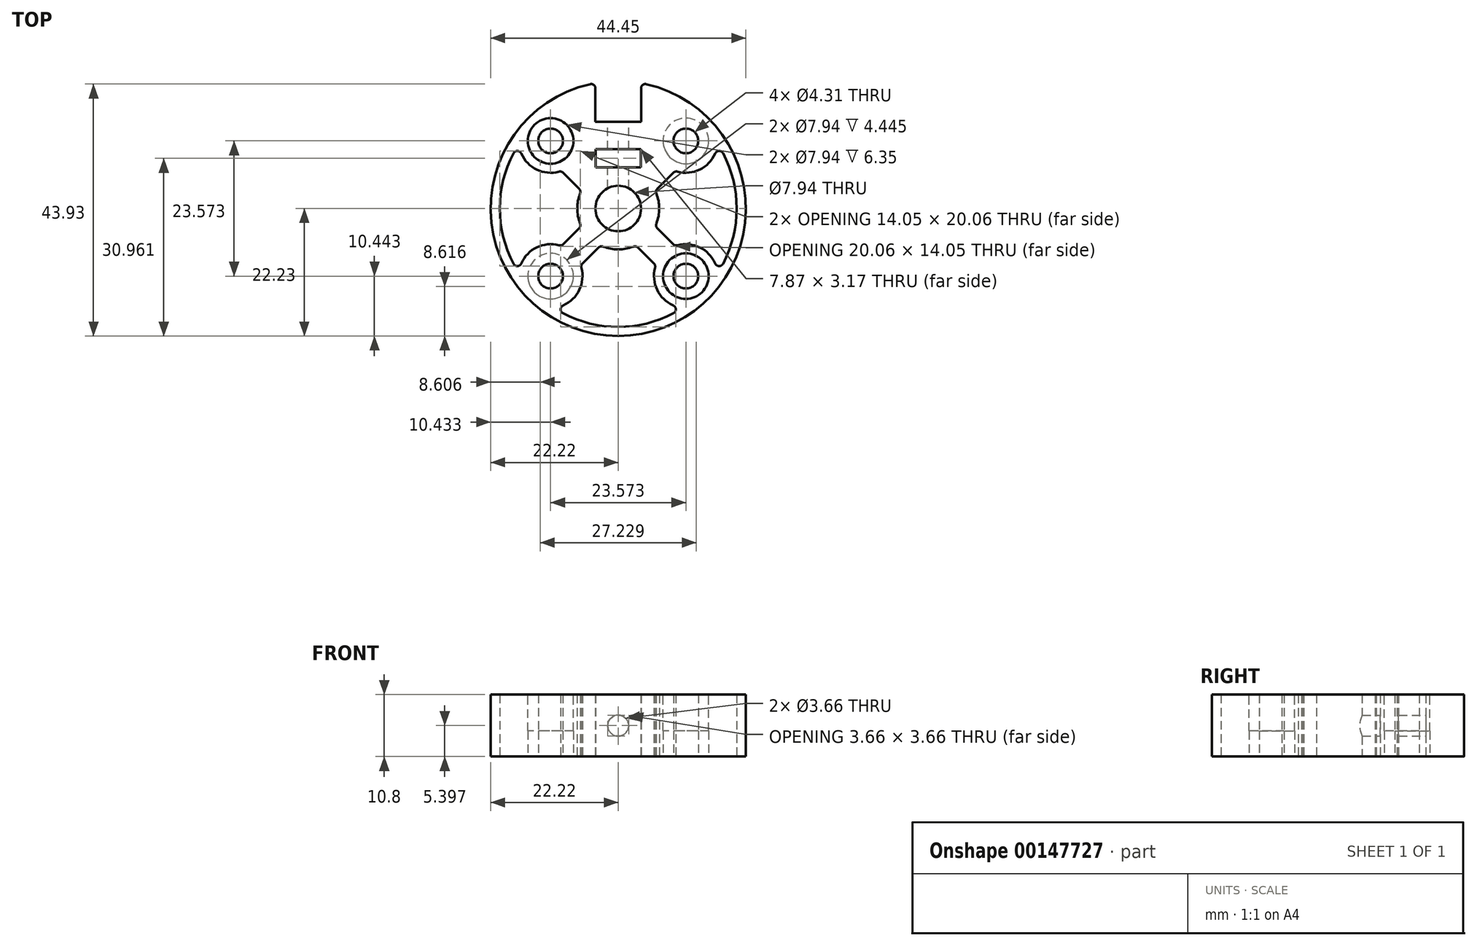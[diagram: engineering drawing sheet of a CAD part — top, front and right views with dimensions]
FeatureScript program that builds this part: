
annotation { "Feature Type Name" : "Feature", "Feature Type Description" : "" }
export const myFeature = defineFeature(function(context is Context, id is Id, definition is map)
    precondition{}
    {
        {
            var Q0;
            Q0=qCreatedBy(makeId("Top.planeOp"),FACE);
            var sketch = newSketch(context, id + "F0", { "sketchPlane" : qUnion([Q0])});
            skCircle(sketch, "E0", {"center": v(0, 0) * mm, "radius": 3.97 * mm});
            skLineSegment(sketch, "E1.bottom", {"start": v(11.79, 11.79) * mm, "end": v(-11.79, 11.79) * mm, "construction": true});
            skLineSegment(sketch, "E1.top", {"start": v(11.79, -11.79) * mm, "end": v(-11.79, -11.79) * mm, "construction": true});
            skLineSegment(sketch, "E1.left", {"start": v(11.79, 11.79) * mm, "end": v(11.79, -11.79) * mm, "construction": true});
            skLineSegment(sketch, "E1.right", {"start": v(-11.79, 11.79) * mm, "end": v(-11.79, -11.79) * mm, "construction": true});
            skCircle(sketch, "E2", {"center": v(-11.79, 11.79) * mm, "radius": 5.56 * mm, "construction": true});
            skLineSegment(sketch, "E3.bottom", {"start": v(-3.97, 21.87) * mm, "end": v(3.97, 21.87) * mm, "construction": true});
            skLineSegment(sketch, "E3.top", {"start": v(-3.97, 15.08) * mm, "end": v(3.97, 15.08) * mm});
            skLineSegment(sketch, "E3.left", {"start": v(-3.97, 21.87) * mm, "end": v(-3.97, 15.08) * mm});
            skLineSegment(sketch, "E3.right", {"start": v(3.97, 21.87) * mm, "end": v(3.97, 15.08) * mm});
            skArc(sketch, "E4", {"start": v(-3.97, 21.87) * mm, "mid": v(0, -22.22) * mm, "end": v(3.97, 21.87) * mm});
            skCircle(sketch, "E5", {"center": v(-11.79, 11.79) * mm, "radius": 2.15 * mm});
            skCircle(sketch, "E6", {"center": v(-11.79, -11.79) * mm, "radius": 2.15 * mm});
            skCircle(sketch, "E7", {"center": v(11.79, -11.79) * mm, "radius": 2.15 * mm});
            skCircle(sketch, "E8", {"center": v(11.79, 11.79) * mm, "radius": 2.15 * mm});
            skLineSegment(sketch, "E9", {"start": v(0, 15.08) * mm, "end": v(0, 10.32) * mm, "construction": true});
            skLineSegment(sketch, "E10", {"start": v(0, 0) * mm, "end": v(0, 2.38) * mm, "construction": true});
            skLineSegment(sketch, "E11", {"start": v(0, 2.38) * mm, "end": v(0, 3.97) * mm, "construction": true});
            skLineSegment(sketch, "E12", {"start": v(0, 3.97) * mm, "end": v(0, 7.14) * mm, "construction": true});
            skLineSegment(sketch, "E13.bottom", {"start": v(3.94, 10.32) * mm, "end": v(-3.94, 10.32) * mm});
            skLineSegment(sketch, "E13.top", {"start": v(3.94, 7.14) * mm, "end": v(-3.94, 7.14) * mm});
            skLineSegment(sketch, "E13.left", {"start": v(3.94, 10.32) * mm, "end": v(3.94, 7.14) * mm});
            skLineSegment(sketch, "E13.right", {"start": v(-3.94, 10.32) * mm, "end": v(-3.94, 7.14) * mm});
            skSolve(sketch);
        }
        {
            var Q0;
            Q0=qSketchRegion(id+"F0",true);
            extrude(context, id + "F1", {"entities" : qUnion([Q0]), "depth" : 10.8 * mm});
        }
        {
            var Q0;
            Q0=makeQuery(id+"F1.opExtrude","SWEPT_FACE",FACE,{"disambiguationData":[OSD([sQuery(id+"F0.wireOp",EDGE,"E3.top")])]});
            var sketch = newSketch(context, id + "F2", { "sketchPlane" : qUnion([Q0])});
            skLineSegment(sketch, "E14", {"start": v(0, 10.8) * mm, "end": v(0, 0) * mm, "construction": true});
            skCircle(sketch, "E15", {"center": v(0, 5.4) * mm, "radius": 1.83 * mm});
            skSolve(sketch);
        }
        {
            var Q0;
            Q0=qSketchRegion(id+"F2",true);
            var Q1;
            Q1=makeQuery(id+"F1.opExtrude","SWEPT_FACE",FACE,{"disambiguationData":[OSD([sQuery(id+"F0.wireOp",EDGE,"E0")])]});
            extrude(context, id + "F3", {"entities" : qUnion([Q0]), "operationType" : NewBodyOperationType.REMOVE, "endBound" : BoundingType.UP_TO_SURFACE, "oppositeDirection" : true, "endBoundEntityFace" : qUnion([Q1]), "depth" : 25.4 * mm});
        }
        {
            var Q0;
            Q0=makeQuery(id+"F1.opExtrude","CAP_FACE",FACE,{"disambiguationData":[OSD([sQuery(id+"F0.wireOp",EDGE,"E0"),sQuery(id+"F0.wireOp",EDGE,"E3.top"),sQuery(id+"F0.wireOp",EDGE,"E3.left"),sQuery(id+"F0.wireOp",EDGE,"E3.right"),sQuery(id+"F0.wireOp",EDGE,"E4"),sQuery(id+"F0.wireOp",EDGE,"E5"),sQuery(id+"F0.wireOp",EDGE,"E6"),sQuery(id+"F0.wireOp",EDGE,"E7"),sQuery(id+"F0.wireOp",EDGE,"E8")])],"isStart":false});
            cPlane(context, id + "F4", {"entities" : qUnion([Q0]), "cplaneType" : CPlaneType.OFFSET, "offset" : 6.35 * mm, "oppositeDirection" : true, "width" : 152.4 * mm, "height" : 152.4 * mm});
        }
        {
            var Q0;
            Q0=makeQuery(id+"F1.opExtrude","CAP_FACE",FACE,{"disambiguationData":[OSD([sQuery(id+"F0.wireOp",EDGE,"E0"),sQuery(id+"F0.wireOp",EDGE,"E3.top"),sQuery(id+"F0.wireOp",EDGE,"E3.left"),sQuery(id+"F0.wireOp",EDGE,"E3.right"),sQuery(id+"F0.wireOp",EDGE,"E4"),sQuery(id+"F0.wireOp",EDGE,"E5"),sQuery(id+"F0.wireOp",EDGE,"E6"),sQuery(id+"F0.wireOp",EDGE,"E7"),sQuery(id+"F0.wireOp",EDGE,"E8")])],"isStart":true});
            var sketch = newSketch(context, id + "F5", { "sketchPlane" : qUnion([Q0])});
            skCircle(sketch, "E16", {"center": v(11.79, -11.79) * mm, "radius": 3.97 * mm});
            skCircle(sketch, "E17", {"center": v(-11.79, 11.79) * mm, "radius": 3.97 * mm});
            skSolve(sketch);
        }
        {
            var Q0;
            Q0=qSketchRegion(id+"F5",true);
            var Q1;
            Q1=qCreatedBy(id+"F4.planeOp",FACE);
            extrude(context, id + "F6", {"entities" : qUnion([Q0]), "operationType" : NewBodyOperationType.REMOVE, "endBound" : BoundingType.UP_TO_SURFACE, "oppositeDirection" : true, "endBoundEntityFace" : qUnion([Q1]), "depth" : 25.4 * mm});
        }
        {
            var Q0;
            Q0=makeQuery(id+"F1.opExtrude","CAP_FACE",FACE,{"disambiguationData":[OSD([sQuery(id+"F0.wireOp",EDGE,"E0"),sQuery(id+"F0.wireOp",EDGE,"E3.top"),sQuery(id+"F0.wireOp",EDGE,"E3.left"),sQuery(id+"F0.wireOp",EDGE,"E3.right"),sQuery(id+"F0.wireOp",EDGE,"E4"),sQuery(id+"F0.wireOp",EDGE,"E5"),sQuery(id+"F0.wireOp",EDGE,"E6"),sQuery(id+"F0.wireOp",EDGE,"E7"),sQuery(id+"F0.wireOp",EDGE,"E8")])],"isStart":true});
            var sketch = newSketch(context, id + "F7", { "sketchPlane" : qUnion([Q0])});
            skArc(sketch, "E18", {"start": v(-9.92, -6.55) * mm, "mid": v(-14.76, -7.1) * mm, "end": v(-17.31, -11.23) * mm});
            skArc(sketch, "E19", {"start": v(-17.31, 11.23) * mm, "mid": v(-14.76, 7.1) * mm, "end": v(-9.92, 6.55) * mm});
            skArc(sketch, "E20", {"start": v(-17.31, 11.23) * mm, "mid": v(-20.64, 0) * mm, "end": v(-17.31, -11.23) * mm});
            skLineSegment(sketch, "E21", {"start": v(-11.79, 11.79) * mm, "end": v(-8.24, 8.24) * mm, "construction": true});
            skLineSegment(sketch, "E22", {"start": v(-11.79, -11.79) * mm, "end": v(-8.24, -8.24) * mm, "construction": true});
            skLineSegment(sketch, "E23", {"start": v(0, 0) * mm, "end": v(-4.76, 4.76) * mm, "construction": true});
            skLineSegment(sketch, "E24", {"start": v(0, 0) * mm, "end": v(-4.76, -4.76) * mm, "construction": true});
            skLineSegment(sketch, "E25.bottom", {"start": v(-6.45, 3.08) * mm, "end": v(-9.92, 6.55) * mm});
            skLineSegment(sketch, "E25.top", {"start": v(-3.08, 6.45) * mm, "end": v(-6.55, 9.92) * mm, "construction": true});
            skLineSegment(sketch, "E25.left", {"start": v(-6.45, 3.08) * mm, "end": v(-3.08, 6.45) * mm, "construction": true});
            skLineSegment(sketch, "E25.right", {"start": v(-9.92, 6.55) * mm, "end": v(-6.55, 9.92) * mm, "construction": true});
            skLineSegment(sketch, "E26.bottom", {"start": v(-6.45, -3.08) * mm, "end": v(-9.92, -6.55) * mm});
            skLineSegment(sketch, "E26.top", {"start": v(-3.08, -6.45) * mm, "end": v(-6.55, -9.92) * mm, "construction": true});
            skLineSegment(sketch, "E26.left", {"start": v(-6.45, -3.08) * mm, "end": v(-3.08, -6.45) * mm, "construction": true});
            skLineSegment(sketch, "E26.right", {"start": v(-9.92, -6.55) * mm, "end": v(-6.55, -9.92) * mm, "construction": true});
            skArc(sketch, "E27", {"start": v(-6.45, 3.08) * mm, "mid": v(-7.14, 0) * mm, "end": v(-6.45, -3.08) * mm});
            skSolve(sketch);
        }
        {
            var Q0;
            Q0=qSketchRegion(id+"F7",true);
            var Q1;
            Q1=makeQuery(id+"F1.opExtrude","CAP_FACE",FACE,{"disambiguationData":[OSD([sQuery(id+"F0.wireOp",EDGE,"E0"),sQuery(id+"F0.wireOp",EDGE,"E3.top"),sQuery(id+"F0.wireOp",EDGE,"E3.left"),sQuery(id+"F0.wireOp",EDGE,"E3.right"),sQuery(id+"F0.wireOp",EDGE,"E4"),sQuery(id+"F0.wireOp",EDGE,"E5"),sQuery(id+"F0.wireOp",EDGE,"E6"),sQuery(id+"F0.wireOp",EDGE,"E7"),sQuery(id+"F0.wireOp",EDGE,"E8")])],"isStart":false});
            extrude(context, id + "F8", {"entities" : qUnion([Q0]), "operationType" : NewBodyOperationType.REMOVE, "endBound" : BoundingType.UP_TO_SURFACE, "oppositeDirection" : true, "endBoundEntityFace" : qUnion([Q1]), "depth" : 25.4 * mm});
        }
        {
            var Q0;
            Q0=makeQuery(id+"F8.boolean.opBoolean","COPY",EDGE,{"derivedFrom":makeQuery(id+"F8.opExtrude","SWEPT_EDGE",EDGE,{"disambiguationData":[OSD([sQuery(id+"F7.wireOp",EDGE,"E19"),sQuery(id+"F7.wireOp",EDGE,"E20")])]})});
            var Q1;
            Q1=makeQuery(id+"F8.boolean.opBoolean","COPY",EDGE,{"derivedFrom":makeQuery(id+"F8.opExtrude","SWEPT_EDGE",EDGE,{"disambiguationData":[OSD([sQuery(id+"F7.wireOp",EDGE,"E19"),sQuery(id+"F7.wireOp",EDGE,"E25.bottom")])]})});
            var Q2;
            Q2=makeQuery(id+"F8.boolean.opBoolean","COPY",EDGE,{"derivedFrom":makeQuery(id+"F8.opExtrude","SWEPT_EDGE",EDGE,{"disambiguationData":[OSD([sQuery(id+"F7.wireOp",EDGE,"E25.bottom"),sQuery(id+"F7.wireOp",EDGE,"E27")])]})});
            var Q3;
            Q3=makeQuery(id+"F8.boolean.opBoolean","COPY",EDGE,{"derivedFrom":makeQuery(id+"F8.opExtrude","SWEPT_EDGE",EDGE,{"disambiguationData":[OSD([sQuery(id+"F7.wireOp",EDGE,"E26.bottom"),sQuery(id+"F7.wireOp",EDGE,"E27")])]})});
            var Q4;
            Q4=makeQuery(id+"F8.boolean.opBoolean","COPY",EDGE,{"derivedFrom":makeQuery(id+"F8.opExtrude","SWEPT_EDGE",EDGE,{"disambiguationData":[OSD([sQuery(id+"F7.wireOp",EDGE,"E18"),sQuery(id+"F7.wireOp",EDGE,"E26.bottom")])]})});
            var Q5;
            Q5=makeQuery(id+"F8.boolean.opBoolean","COPY",EDGE,{"derivedFrom":makeQuery(id+"F8.opExtrude","SWEPT_EDGE",EDGE,{"disambiguationData":[OSD([sQuery(id+"F7.wireOp",EDGE,"E18"),sQuery(id+"F7.wireOp",EDGE,"E20")])]})});
            var Q6;
            Q6=makeQuery(id+"F1.opExtrude","SWEPT_EDGE",EDGE,{"disambiguationData":[OSD([sQuery(id+"F0.wireOp",EDGE,"E3.right"),sQuery(id+"F0.wireOp",EDGE,"E4")])]});
            var Q7;
            Q7=makeQuery(id+"F1.opExtrude","SWEPT_EDGE",EDGE,{"disambiguationData":[OSD([sQuery(id+"F0.wireOp",EDGE,"E3.left"),sQuery(id+"F0.wireOp",EDGE,"E4")])]});
            fillet(context, id + "F9", {"entities" : qUnion([Q0, Q1, Q2, Q3, Q4, Q5, Q6, Q7]), "radius" : 0.76 * mm, "tangentPropagation" : true, "allowEdgeOverflow" : false});
        }
        {
            var Q0;
            Q0=makeQuery(id+"F9.opFillet","BLEND_FACE",FACE,{"disambiguationData":[OSD([sQuery(id+"F7.wireOp",EDGE,"E19"),sQuery(id+"F7.wireOp",EDGE,"E25.bottom")])]});
            var Q1;
            Q1=makeQuery(id+"F8.boolean.opBoolean","COPY",FACE,{"derivedFrom":makeQuery(id+"F8.opExtrude","SWEPT_FACE",FACE,{"disambiguationData":[OSD([sQuery(id+"F7.wireOp",EDGE,"E25.bottom")])]})});
            var Q2;
            Q2=makeQuery(id+"F9.opFillet","BLEND_FACE",FACE,{"disambiguationData":[OSD([sQuery(id+"F7.wireOp",EDGE,"E25.bottom"),sQuery(id+"F7.wireOp",EDGE,"E27")])]});
            var Q3;
            Q3=makeQuery(id+"F8.boolean.opBoolean","COPY",FACE,{"derivedFrom":makeQuery(id+"F8.opExtrude","SWEPT_FACE",FACE,{"disambiguationData":[OSD([sQuery(id+"F7.wireOp",EDGE,"E27")])]})});
            var Q4;
            Q4=makeQuery(id+"F9.opFillet","BLEND_FACE",FACE,{"disambiguationData":[OSD([sQuery(id+"F7.wireOp",EDGE,"E26.bottom"),sQuery(id+"F7.wireOp",EDGE,"E27")])]});
            var Q5;
            Q5=makeQuery(id+"F8.boolean.opBoolean","COPY",FACE,{"derivedFrom":makeQuery(id+"F8.opExtrude","SWEPT_FACE",FACE,{"disambiguationData":[OSD([sQuery(id+"F7.wireOp",EDGE,"E26.bottom")])]})});
            var Q6;
            Q6=makeQuery(id+"F9.opFillet","BLEND_FACE",FACE,{"disambiguationData":[OSD([sQuery(id+"F7.wireOp",EDGE,"E18"),sQuery(id+"F7.wireOp",EDGE,"E26.bottom")])]});
            var Q7;
            Q7=makeQuery(id+"F8.boolean.opBoolean","COPY",FACE,{"derivedFrom":makeQuery(id+"F8.opExtrude","SWEPT_FACE",FACE,{"disambiguationData":[OSD([sQuery(id+"F7.wireOp",EDGE,"E18")])]})});
            var Q8;
            Q8=makeQuery(id+"F9.opFillet","BLEND_FACE",FACE,{"disambiguationData":[OSD([sQuery(id+"F7.wireOp",EDGE,"E18"),sQuery(id+"F7.wireOp",EDGE,"E20")])]});
            var Q9;
            Q9=makeQuery(id+"F8.boolean.opBoolean","COPY",FACE,{"derivedFrom":makeQuery(id+"F8.opExtrude","SWEPT_FACE",FACE,{"disambiguationData":[OSD([sQuery(id+"F7.wireOp",EDGE,"E20")])]})});
            var Q10;
            Q10=makeQuery(id+"F9.opFillet","BLEND_FACE",FACE,{"disambiguationData":[OSD([sQuery(id+"F7.wireOp",EDGE,"E19"),sQuery(id+"F7.wireOp",EDGE,"E20")])]});
            var Q11;
            Q11=makeQuery(id+"F8.boolean.opBoolean","COPY",FACE,{"derivedFrom":makeQuery(id+"F8.opExtrude","SWEPT_FACE",FACE,{"disambiguationData":[OSD([sQuery(id+"F7.wireOp",EDGE,"E19")])]})});
            var Q12;
            Q12=makeQuery(id+"F1.opExtrude","SWEPT_FACE",FACE,{"disambiguationData":[OSD([sQuery(id+"F0.wireOp",EDGE,"E0")])]});
            circularPattern(context, id + "F10", {"patternType" : PatternType.FACE, "faces" : qUnion([Q0, Q1, Q2, Q3, Q4, Q5, Q6, Q7, Q8, Q9, Q10, Q11]), "axis" : qUnion([Q12]), "angle" : 90 * degree, "instanceCount" : 3});
        }
        {
            var Q0;
            Q0=makeQuery(id+"F1.opExtrude","CAP_FACE",FACE,{"disambiguationData":[OSD([sQuery(id+"F0.wireOp",EDGE,"E0"),sQuery(id+"F0.wireOp",EDGE,"E3.top"),sQuery(id+"F0.wireOp",EDGE,"E3.left"),sQuery(id+"F0.wireOp",EDGE,"E3.right"),sQuery(id+"F0.wireOp",EDGE,"E4"),sQuery(id+"F0.wireOp",EDGE,"E5"),sQuery(id+"F0.wireOp",EDGE,"E6"),sQuery(id+"F0.wireOp",EDGE,"E7"),sQuery(id+"F0.wireOp",EDGE,"E8"),sQuery(id+"F0.wireOp",EDGE,"E13.bottom"),sQuery(id+"F0.wireOp",EDGE,"E13.top"),sQuery(id+"F0.wireOp",EDGE,"E13.left"),sQuery(id+"F0.wireOp",EDGE,"E13.right")])],"isStart":false});
            var sketch = newSketch(context, id + "F11", { "sketchPlane" : qUnion([Q0])});
            skCircle(sketch, "E28", {"center": v(-11.79, 11.79) * mm, "radius": 3.97 * mm});
            skCircle(sketch, "E29", {"center": v(11.79, -11.79) * mm, "radius": 3.97 * mm});
            skSolve(sketch);
        }
        {
            var Q0;
            Q0=makeQuery(id+"F1.opExtrude","CAP_FACE",FACE,{"disambiguationData":[OSD([sQuery(id+"F0.wireOp",EDGE,"E0"),sQuery(id+"F0.wireOp",EDGE,"E3.top"),sQuery(id+"F0.wireOp",EDGE,"E3.left"),sQuery(id+"F0.wireOp",EDGE,"E3.right"),sQuery(id+"F0.wireOp",EDGE,"E4"),sQuery(id+"F0.wireOp",EDGE,"E5"),sQuery(id+"F0.wireOp",EDGE,"E6"),sQuery(id+"F0.wireOp",EDGE,"E7"),sQuery(id+"F0.wireOp",EDGE,"E8"),sQuery(id+"F0.wireOp",EDGE,"E13.bottom"),sQuery(id+"F0.wireOp",EDGE,"E13.top"),sQuery(id+"F0.wireOp",EDGE,"E13.left"),sQuery(id+"F0.wireOp",EDGE,"E13.right")])],"isStart":true});
            cPlane(context, id + "F12", {"entities" : qUnion([Q0]), "cplaneType" : CPlaneType.OFFSET, "offset" : 4.44 * mm, "oppositeDirection" : true, "width" : 152.4 * mm, "height" : 152.4 * mm});
        }
        {
            var Q0;
            Q0=makeQuery(id+"F11.imprint","IMPRINT",FACE,{"disambiguationData":[TD([[makeQuery(id+"F11.imprint","IMPRINT",EDGE,{"derivedFrom":sQuery(id+"F11.wireOp",EDGE,"E28")}),1.0]])]});
            var Q1;
            Q1=makeQuery(id+"F11.imprint","IMPRINT",FACE,{"disambiguationData":[TD([[makeQuery(id+"F11.imprint","IMPRINT",EDGE,{"derivedFrom":sQuery(id+"F11.wireOp",EDGE,"E29")}),1.0]])]});
            var Q2;
            Q2=qCreatedBy(id+"F12.planeOp",FACE);
            extrude(context, id + "F13", {"entities" : qUnion([Q0, Q1]), "operationType" : NewBodyOperationType.REMOVE, "endBound" : BoundingType.UP_TO_SURFACE, "oppositeDirection" : true, "endBoundEntityFace" : qUnion([Q2]), "depth" : 25.4 * mm});
        }
    });
